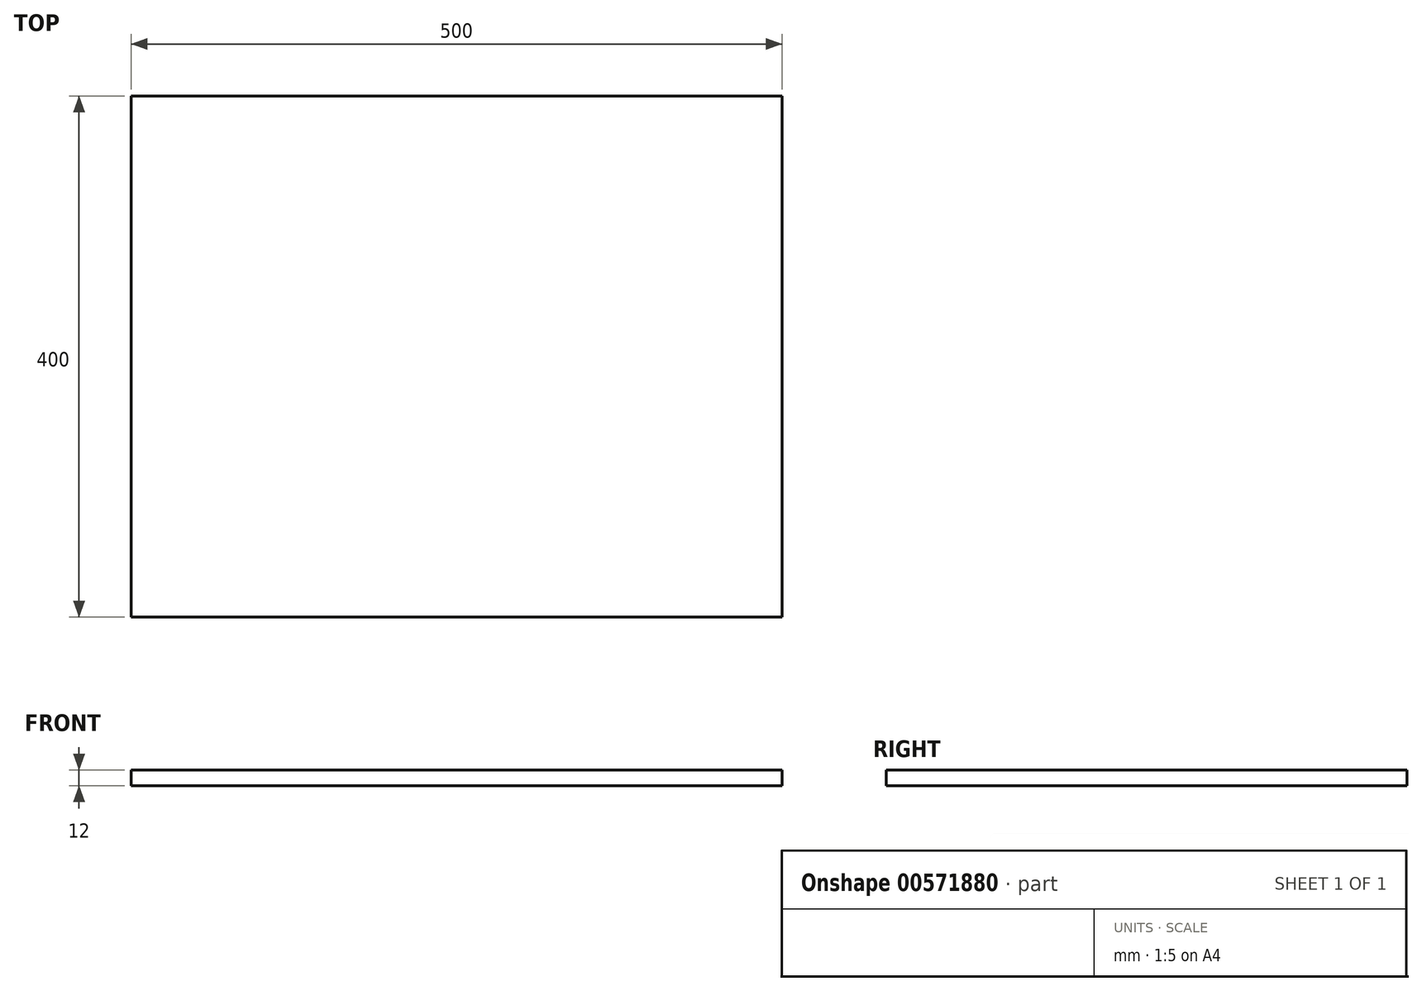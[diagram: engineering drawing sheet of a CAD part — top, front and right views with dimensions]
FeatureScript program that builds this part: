
annotation { "Feature Type Name" : "Feature", "Feature Type Description" : "" }
export const myFeature = defineFeature(function(context is Context, id is Id, definition is map)
    precondition{}
    {
        {
            var Q0;
            Q0=qCreatedBy(makeId("Top.planeOp"),FACE);
            var sketch = newSketch(context, id + "F0", { "sketchPlane" : qUnion([Q0])});
            skLineSegment(sketch, "E0.bottom", {"start": v(-480.53, 226.26) * mm, "end": v(19.47, 226.26) * mm});
            skLineSegment(sketch, "E0.top", {"start": v(-480.53, -173.74) * mm, "end": v(19.47, -173.74) * mm});
            skLineSegment(sketch, "E0.left", {"start": v(-480.53, 226.26) * mm, "end": v(-480.53, -173.74) * mm});
            skLineSegment(sketch, "E0.right", {"start": v(19.47, 226.26) * mm, "end": v(19.47, -173.74) * mm});
            skSolve(sketch);
        }
        {
            var Q0;
            Q0=makeQuery(id+"F0.imprint","IMPRINT",FACE,{"disambiguationData":[TD([[makeQuery(id+"F0.imprint","IMPRINT",EDGE,{"derivedFrom":sQuery(id+"F0.wireOp",EDGE,"E0.bottom")}),-1.0]])]});
            extrude(context, id + "F1", {"entities" : qUnion([Q0]), "depth" : 12 * mm, "offsetDistance" : 25 * mm});
        }
    });
